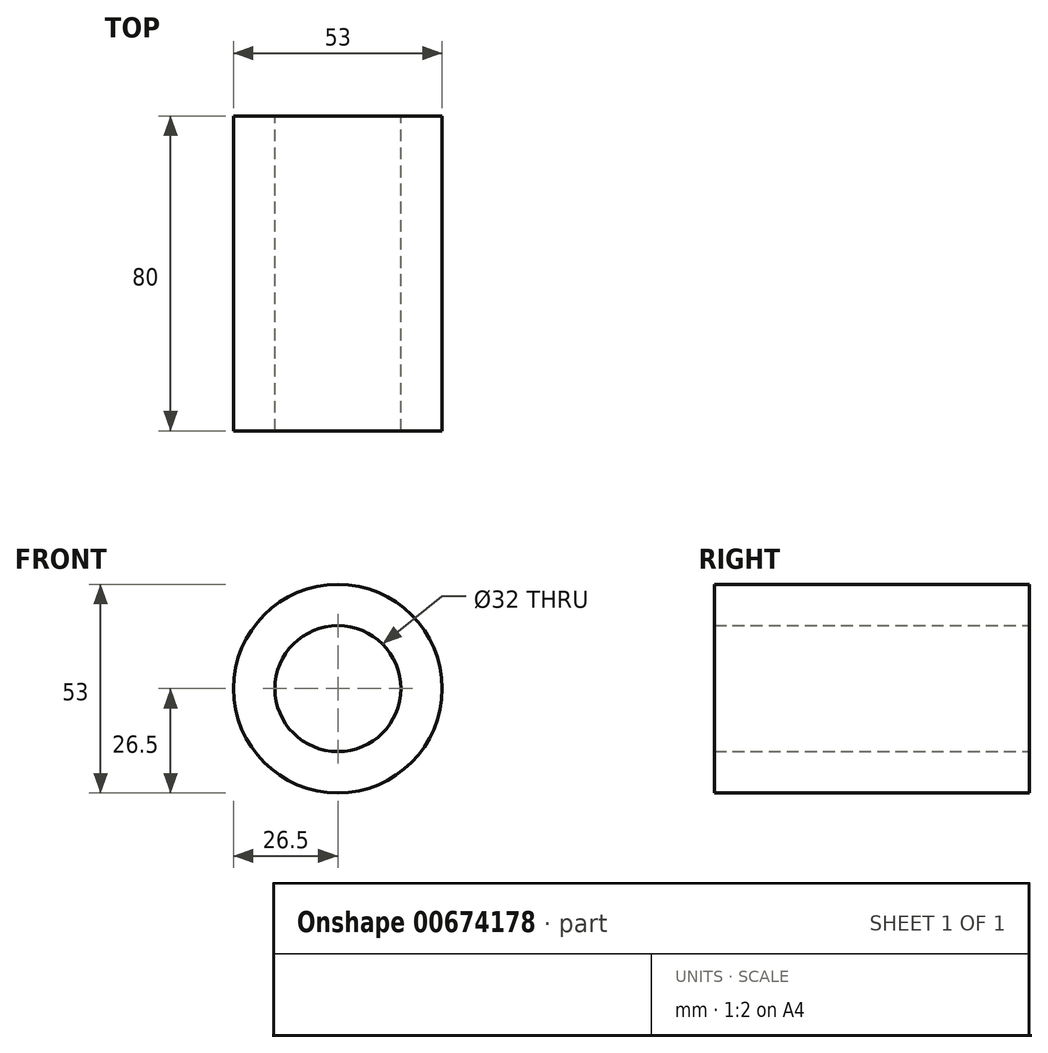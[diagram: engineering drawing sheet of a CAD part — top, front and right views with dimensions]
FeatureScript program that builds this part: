
annotation { "Feature Type Name" : "Feature", "Feature Type Description" : "" }
export const myFeature = defineFeature(function(context is Context, id is Id, definition is map)
    precondition{}
    {
        {
            var Q0;
            Q0=qCreatedBy(makeId("Front.planeOp"),FACE);
            var sketch = newSketch(context, id + "F0", { "sketchPlane" : qUnion([Q0])});
            skCircle(sketch, "E0", {"center": v(0, 0) * mm, "radius": 26.5 * mm});
            skCircle(sketch, "E1", {"center": v(0, 0) * mm, "radius": 16 * mm});
            skSolve(sketch);
        }
        {
            var Q0;
            Q0=makeQuery(id+"F0.imprint","IMPRINT",FACE,{"disambiguationData":[TD([[makeQuery(id+"F0.imprint","IMPRINT",EDGE,{"derivedFrom":sQuery(id+"F0.wireOp",EDGE,"E0")}),1.0]])]});
            extrude(context, id + "F1", {"entities" : qUnion([Q0]), "depth" : 80 * mm, "offsetDistance" : 25 * mm});
        }
    });
